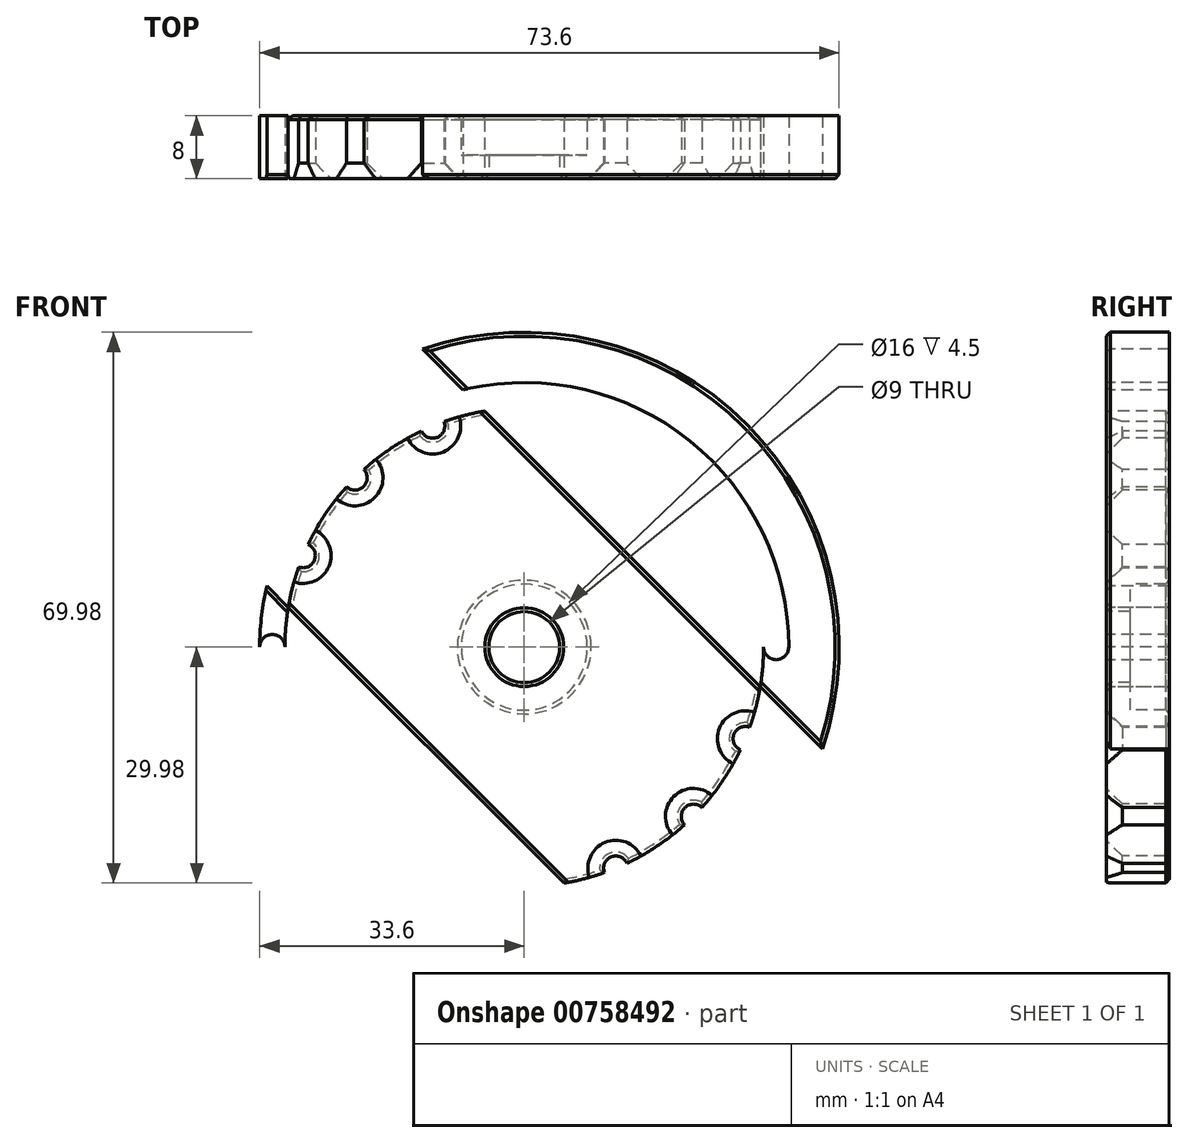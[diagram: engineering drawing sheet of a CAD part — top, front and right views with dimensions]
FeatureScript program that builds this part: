
annotation { "Feature Type Name" : "Feature", "Feature Type Description" : "" }
export const myFeature = defineFeature(function(context is Context, id is Id, definition is map)
    precondition{}
    {
        {
            var Q0;
            Q0=qCreatedBy(makeId("Front.planeOp"),FACE);
            var sketch = newSketch(context, id + "F0", { "sketchPlane" : qUnion([Q0])});
            skCircle(sketch, "E0", {"center": v(0, 0) * mm, "radius": 4.5 * mm});
            skCircle(sketch, "E1", {"center": v(0, 0) * mm, "radius": 40 * mm});
            skCircle(sketch, "E2", {"center": v(-32, 0) * mm, "radius": 1.6 * mm});
            skCircle(sketch, "E3.1.0", {"center": v(0, -32) * mm, "radius": 1.6 * mm});
            skCircle(sketch, "E3.2.0", {"center": v(32, 0) * mm, "radius": 1.6 * mm});
            skCircle(sketch, "E3.3.0", {"center": v(0, 32) * mm, "radius": 1.6 * mm});
            skCircle(sketch, "E4", {"center": v(0, 0) * mm, "radius": 8 * mm});
            skCircle(sketch, "E5", {"center": v(0, 0) * mm, "radius": 25 * mm});
            skCircle(sketch, "E6", {"center": v(0, 0) * mm, "radius": 33.6 * mm});
            skCircle(sketch, "E7", {"center": v(0, 0) * mm, "radius": 30.4 * mm});
            skCircle(sketch, "E8", {"center": v(-11.63, 28.09) * mm, "radius": 1.55 * mm});
            skCircle(sketch, "E9", {"center": v(-21.5, 21.5) * mm, "radius": 1.55 * mm});
            skLineSegment(sketch, "E10", {"start": v(0, 0) * mm, "end": v(-21.5, 21.5) * mm, "construction": true});
            skLineSegment(sketch, "E11", {"start": v(0, 0) * mm, "end": v(-11.63, 28.09) * mm, "construction": true});
            skCircle(sketch, "E12.MirrorC", {"center": v(-28.09, 11.63) * mm, "radius": 1.55 * mm});
            skCircle(sketch, "E13.1.0", {"center": v(11.63, -28.09) * mm, "radius": 1.55 * mm});
            skCircle(sketch, "E13.1.1", {"center": v(21.5, -21.5) * mm, "radius": 1.55 * mm});
            skCircle(sketch, "E13.1.2", {"center": v(28.09, -11.63) * mm, "radius": 1.55 * mm});
            skLineSegment(sketch, "E14", {"start": v(-11.63, 28.09) * mm, "end": v(28.09, -11.63) * mm, "construction": true});
            skLineSegment(sketch, "E15", {"start": v(-12.92, 37.86) * mm, "end": v(37.86, -12.92) * mm});
            skLineSegment(sketch, "E16.MirrorCS", {"start": v(-37.86, 12.92) * mm, "end": v(12.92, -37.86) * mm});
            skSolve(sketch);
        }
        {
            var Q0;
            {var subQ0=sQuery(id+"F0.wireOp",EDGE,"E15");var subQ1=sQuery(id+"F0.wireOp",EDGE,"E1");var subQ2=makeQuery(id+"F0.imprint","INTERSECT",VERTEX,{"disambiguationData":[OD(0.0)],"derivedFrom":[subQ1,subQ0]});Q0=makeQuery(id+"F0.imprint","IMPRINT",FACE,{"disambiguationData":[TD([[makeQuery(id+"F0.imprint","IMPRINT",EDGE,{"disambiguationData":[TD([[subQ2,-1.0]])],"derivedFrom":subQ1}),1.0]])]});}
            var Q1;
            {var subQ5=sQuery(id+"F0.wireOp",EDGE,"E15");var subQ12=sQuery(id+"F0.wireOp",EDGE,"E6");var subQ13=makeQuery(id+"F0.imprint","INTERSECT",VERTEX,{"disambiguationData":[OD(0.0)],"derivedFrom":[subQ12,subQ5]});Q1=makeQuery(id+"F0.imprint","IMPRINT",FACE,{"disambiguationData":[TD([[makeQuery(id+"F0.imprint","IMPRINT",EDGE,{"disambiguationData":[TD([[subQ13,-1.0]])],"derivedFrom":subQ12}),1.0]])]});}
            var Q2;
            {var subQ5=sQuery(id+"F0.wireOp",EDGE,"E15");var subQ11=sQuery(id+"F0.wireOp",EDGE,"E5");var subQ12=makeQuery(id+"F0.imprint","INTERSECT",VERTEX,{"disambiguationData":[OD(0.0)],"derivedFrom":[subQ11,subQ5]});Q2=makeQuery(id+"F0.imprint","IMPRINT",FACE,{"disambiguationData":[TD([[makeQuery(id+"F0.imprint","IMPRINT",EDGE,{"disambiguationData":[TD([[subQ12,-1.0]])],"derivedFrom":subQ11}),-1.0]])]});}
            var Q3;
            Q3=makeQuery(id+"F0.imprint","IMPRINT",FACE,{"disambiguationData":[TD([[makeQuery(id+"F0.imprint","IMPRINT",EDGE,{"derivedFrom":sQuery(id+"F0.wireOp",EDGE,"E4")}),-1.0]])]});
            var Q4;
            {var subQ5=sQuery(id+"F0.wireOp",EDGE,"E15");var subQ6=sQuery(id+"F0.wireOp",EDGE,"E5");var subQ7=makeQuery(id+"F0.imprint","INTERSECT",VERTEX,{"disambiguationData":[OD(1.0)],"derivedFrom":[subQ6,subQ5]});Q4=makeQuery(id+"F0.imprint","IMPRINT",FACE,{"disambiguationData":[TD([[makeQuery(id+"F0.imprint","IMPRINT",EDGE,{"disambiguationData":[TD([[subQ7,1.0]])],"derivedFrom":subQ6}),-1.0]])]});}
            var Q5;
            {var subQ8=sQuery(id+"F0.wireOp",EDGE,"E16.MirrorCS");var subQ11=sQuery(id+"F0.wireOp",EDGE,"E6");var subQ12=makeQuery(id+"F0.imprint","INTERSECT",VERTEX,{"disambiguationData":[OD(1.0)],"derivedFrom":[subQ11,subQ8]});Q5=makeQuery(id+"F0.imprint","IMPRINT",FACE,{"disambiguationData":[TD([[makeQuery(id+"F0.imprint","IMPRINT",EDGE,{"disambiguationData":[TD([[subQ12,-1.0]])],"derivedFrom":subQ11}),1.0]])]});}
            var Q6;
            {var subQ0=sQuery(id+"F0.wireOp",EDGE,"E15");var subQ1=sQuery(id+"F0.wireOp",EDGE,"E1");var subQ2=makeQuery(id+"F0.imprint","INTERSECT",VERTEX,{"disambiguationData":[OD(1.0)],"derivedFrom":[subQ1,subQ0]});Q6=makeQuery(id+"F0.imprint","IMPRINT",FACE,{"disambiguationData":[TD([[makeQuery(id+"F0.imprint","IMPRINT",EDGE,{"disambiguationData":[TD([[subQ2,1.0]])],"derivedFrom":subQ1}),1.0]])]});}
            extrude(context, id + "F1", {"entities" : qUnion([Q0, Q1, Q2, Q3, Q4, Q5, Q6]), "oppositeDirection" : true, "depth" : 8 * mm, "offsetDistance" : 25 * mm});
        }
        {
            var Q0;
            Q0=makeQuery(id+"F0.imprint","IMPRINT",FACE,{"disambiguationData":[TD([[makeQuery(id+"F0.imprint","IMPRINT",EDGE,{"derivedFrom":sQuery(id+"F0.wireOp",EDGE,"E0")}),-1.0]])]});
            extrude(context, id + "F2", {"entities" : qUnion([Q0]), "operationType" : NewBodyOperationType.ADD, "oppositeDirection" : true, "depth" : 3 * mm, "offsetDistance" : 25 * mm});
        }
        {
            var Q0;
            Q0=makeQuery(id+"F1.opExtrude","CAP_FACE",FACE,{"disambiguationData":[OSD([sQuery(id+"F0.wireOp",EDGE,"E1"),sQuery(id+"F0.wireOp",EDGE,"E2"),sQuery(id+"F0.wireOp",EDGE,"E3.1.0"),sQuery(id+"F0.wireOp",EDGE,"E3.2.0"),sQuery(id+"F0.wireOp",EDGE,"E3.3.0"),sQuery(id+"F0.wireOp",EDGE,"E4"),sQuery(id+"F0.wireOp",EDGE,"E6"),sQuery(id+"F0.wireOp",EDGE,"E7"),sQuery(id+"F0.wireOp",EDGE,"E8"),sQuery(id+"F0.wireOp",EDGE,"E9"),sQuery(id+"F0.wireOp",EDGE,"E12.MirrorC"),sQuery(id+"F0.wireOp",EDGE,"E13.1.0"),sQuery(id+"F0.wireOp",EDGE,"E13.1.1"),sQuery(id+"F0.wireOp",EDGE,"E13.1.2")])],"isStart":false});
            var Q1;
            Q1=makeQuery(id+"F2.opExtrude","CAP_EDGE",EDGE,{"disambiguationData":[OSD([sQuery(id+"F0.wireOp",EDGE,"E0")])],"isStart":true});
            var Q2;
            Q2=makeQuery(id+"F1.opExtrude","CAP_EDGE",EDGE,{"disambiguationData":[OSD([sQuery(id+"F0.wireOp",EDGE,"E15")])],"isStart":true});
            var Q3;
            {var subQ0=sQuery(id+"F0.wireOp",EDGE,"E1");Q3=makeQuery(id+"F1.opExtrude","CAP_EDGE",EDGE,{"disambiguationData":[OSD([subQ0]),TDD([makeQuery(id+"F0.imprint","IMPRINT",EDGE,{"disambiguationData":[TD([[makeQuery(id+"F0.imprint","INTERSECT",VERTEX,{"disambiguationData":[OD(0.0)],"derivedFrom":[subQ0,sQuery(id+"F0.wireOp",EDGE,"E15")]}),-1.0]])],"derivedFrom":subQ0})])],"isStart":true});}
            var Q4;
            Q4=makeQuery(id+"F1.opExtrude","CAP_EDGE",EDGE,{"disambiguationData":[OSD([sQuery(id+"F0.wireOp",EDGE,"E16.MirrorCS")])],"isStart":true});
            var Q5;
            {var subQ0=sQuery(id+"F0.wireOp",EDGE,"E1");Q5=makeQuery(id+"F1.opExtrude","CAP_EDGE",EDGE,{"disambiguationData":[OSD([subQ0]),TDD([makeQuery(id+"F0.imprint","IMPRINT",EDGE,{"disambiguationData":[TD([[makeQuery(id+"F0.imprint","INTERSECT",VERTEX,{"disambiguationData":[OD(1.0)],"derivedFrom":[subQ0,sQuery(id+"F0.wireOp",EDGE,"E15")]}),1.0]])],"derivedFrom":subQ0})])],"isStart":true});}
            chamfer(context, id + "F3", {"entities" : qUnion([Q0, Q1, Q2, Q3, Q4, Q5]), "width" : 0.5 * mm, "tangentPropagation" : true});
        }
        {
            var Q0;
            Q0=makeQuery(id+"F1.opExtrude","CAP_EDGE",EDGE,{"disambiguationData":[OSD([sQuery(id+"F0.wireOp",EDGE,"E12.MirrorC")])],"isStart":true});
            var Q1;
            Q1=makeQuery(id+"F1.opExtrude","CAP_EDGE",EDGE,{"disambiguationData":[OSD([sQuery(id+"F0.wireOp",EDGE,"E9")])],"isStart":true});
            var Q2;
            Q2=makeQuery(id+"F1.opExtrude","CAP_EDGE",EDGE,{"disambiguationData":[OSD([sQuery(id+"F0.wireOp",EDGE,"E8")])],"isStart":true});
            var Q3;
            Q3=makeQuery(id+"F1.opExtrude","CAP_EDGE",EDGE,{"disambiguationData":[OSD([sQuery(id+"F0.wireOp",EDGE,"E13.1.2")])],"isStart":true});
            var Q4;
            Q4=makeQuery(id+"F1.opExtrude","CAP_EDGE",EDGE,{"disambiguationData":[OSD([sQuery(id+"F0.wireOp",EDGE,"E13.1.1")])],"isStart":true});
            var Q5;
            Q5=makeQuery(id+"F1.opExtrude","CAP_EDGE",EDGE,{"disambiguationData":[OSD([sQuery(id+"F0.wireOp",EDGE,"E13.1.0")])],"isStart":true});
            chamfer(context, id + "F4", {"entities" : qUnion([Q0, Q1, Q2, Q3, Q4, Q5]), "width" : 2 * mm, "tangentPropagation" : true});
        }
    });
